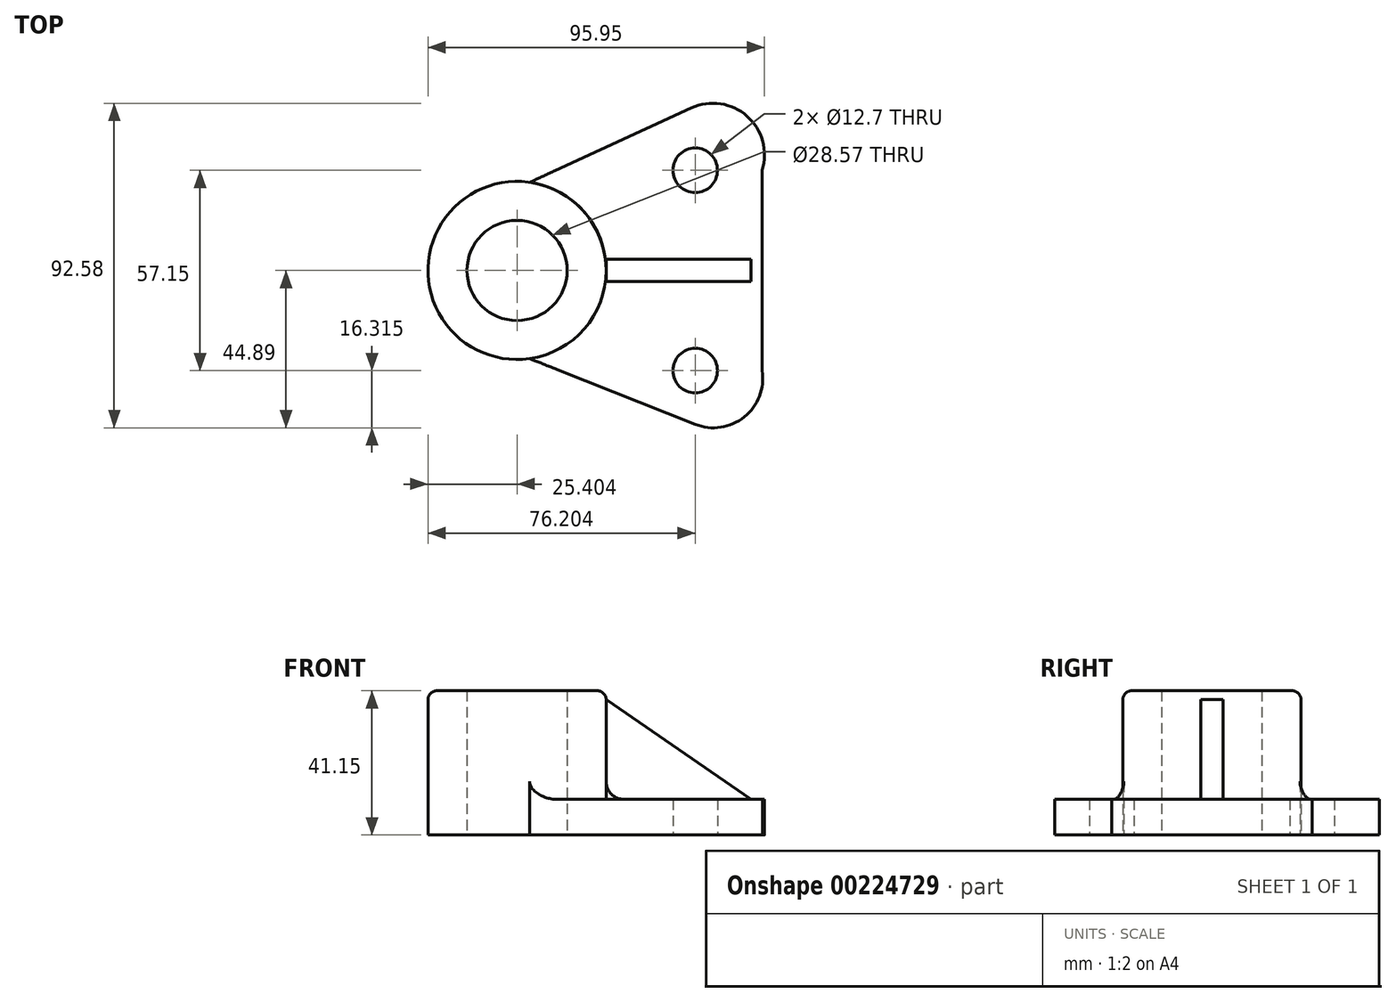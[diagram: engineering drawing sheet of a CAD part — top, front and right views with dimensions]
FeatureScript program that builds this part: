
annotation { "Feature Type Name" : "Feature", "Feature Type Description" : "" }
export const myFeature = defineFeature(function(context is Context, id is Id, definition is map)
    precondition{}
    {
        {
            var Q0;
            Q0=qCreatedBy(makeId("Top.planeOp"),FACE);
            var sketch = newSketch(context, id + "F0", { "sketchPlane" : qUnion([Q0])});
            skCircle(sketch, "E0", {"center": v(-38.75, 0) * mm, "radius": 14.29 * mm});
            skCircle(sketch, "E1", {"center": v(-38.75, 0) * mm, "radius": 25.4 * mm});
            skCircle(sketch, "E2", {"center": v(12.05, -28.58) * mm, "radius": 6.35 * mm});
            skCircle(sketch, "E3", {"center": v(12.05, 28.58) * mm, "radius": 6.35 * mm});
            skLineSegment(sketch, "E4", {"start": v(-35.16, 25.15) * mm, "end": v(11, 46.36) * mm});
            skLineSegment(sketch, "E5", {"start": v(-35.16, -25.15) * mm, "end": v(12.05, -43.9) * mm});
            skLineSegment(sketch, "E6", {"start": v(31.1, 28.58) * mm, "end": v(12.05, 28.58) * mm});
            skLineSegment(sketch, "E7", {"start": v(12.05, -28.58) * mm, "end": v(31.1, -28.58) * mm});
            skLineSegment(sketch, "E8", {"start": v(31.1, 28.58) * mm, "end": v(31.1, -28.58) * mm});
            skArc(sketch, "E9", {"start": v(11, 46.36) * mm, "mid": v(26.84, 44.01) * mm, "end": v(31.1, 28.58) * mm});
            skArc(sketch, "E10", {"start": v(12.05, -43.9) * mm, "mid": v(26.04, -41.79) * mm, "end": v(31.1, -28.58) * mm});
            skSolve(sketch);
        }
        {
            var Q0;
            Q0=qCreatedBy(makeId("Top.planeOp"),FACE);
            var sketch = newSketch(context, id + "F1", { "sketchPlane" : qUnion([Q0])});
            skSolve(sketch);
        }
        {
            var Q0;
            Q0 = qSketchRegion(id + "F1", true);
            var Q1;
            Q1=makeQuery(id+"F0.imprint","IMPRINT",FACE,{"disambiguationData":[TD([[makeQuery(id+"F0.imprint","IMPRINT",EDGE,{"derivedFrom":sQuery(id+"F0.wireOp",EDGE,"E0")}),-1.0]])]});
            extrude(context, id + "F2", {"entities" : qUnion([Q0, Q1]), "depth" : 41.15 * mm});
        }
        {
            var Q0;
            Q0 = qSketchRegion(id + "F0", true);
            extrude(context, id + "F3", {"entities" : qUnion([Q0]), "operationType" : NewBodyOperationType.ADD, "depth" : 10.16 * mm});
        }
        {
            var Q0;
            Q0=makeQuery(id+"F2.opExtrude","CAP_EDGE",EDGE,{"disambiguationData":[OSD([sQuery(id+"F0.wireOp",EDGE,"E1")])],"isStart":false});
            fillet(context, id + "F4", {"entities" : qUnion([Q0]), "radius" : 2.54 * mm, "tangentPropagation" : true, "allowEdgeOverflow" : false});
        }
        {
            var Q0;
            Q0=qCreatedBy(makeId("Front.planeOp"),FACE);
            var sketch = newSketch(context, id + "F5", { "sketchPlane" : qUnion([Q0])});
            skLineSegment(sketch, "E11.0.1", {"start": v(11, 10.16) * mm, "end": v(12.05, 10.16) * mm});
            skLineSegment(sketch, "E11.0.4", {"start": v(31.8, 10.16) * mm, "end": v(31.29, 10.16) * mm});
            skLineSegment(sketch, "E12", {"start": v(-13.35, 38.6) * mm, "end": v(-13.35, 10.16) * mm});
            skLineSegment(sketch, "E13.trimOffspring", {"start": v(12.05, 10.16) * mm, "end": v(11, 10.16) * mm});
            skPoint(sketch, "E11.0.0.end.orphan", {"position": v(-13.35, 10.16) * mm});
            skPoint(sketch, "E14.orphan", {"position": v(-35.16, 10.16) * mm});
            skLineSegment(sketch, "E15", {"start": v(-13.35, 10.16) * mm, "end": v(27.99, 10.16) * mm});
            skLineSegment(sketch, "E16", {"start": v(27.99, 10.16) * mm, "end": v(-13.35, 38.6) * mm});
            skSolve(sketch);
        }
        {
            var Q0;
            Q0 = qSketchRegion(id + "F5", true);
            extrude(context, id + "F6", {"entities" : qUnion([Q0]), "depth" : 3.17 * mm, "hasSecondDirection" : true, "secondDirectionOppositeDirection" : true, "secondDirectionDepth" : 3.17 * mm});
        }
        {
            var Q0;
            {var subQ0=sQuery(id+"F0.wireOp",EDGE,"E1");Q0=makeQuery(id+"F3.boolean.opBoolean","INTERSECT",EDGE,{"derivedFrom":[makeQuery(id+"F2.opExtrude","SWEPT_FACE",FACE,{"disambiguationData":[OSD([subQ0])]}),makeQuery(id+"F3.opExtrude","CAP_FACE",FACE,{"disambiguationData":[OSD([sQuery(id+"F0.wireOp",EDGE,"E0"),subQ0,sQuery(id+"F0.wireOp",EDGE,"E2"),sQuery(id+"F0.wireOp",EDGE,"E3"),sQuery(id+"F0.wireOp",EDGE,"E4"),sQuery(id+"F0.wireOp",EDGE,"E5"),sQuery(id+"F0.wireOp",EDGE,"E8"),sQuery(id+"F0.wireOp",EDGE,"E9"),sQuery(id+"F0.wireOp",EDGE,"E10")])],"isStart":false})]});}
            fillet(context, id + "F7", {"entities" : qUnion([Q0]), "radius" : 5.08 * mm, "tangentPropagation" : true, "allowEdgeOverflow" : false});
        }
    });
